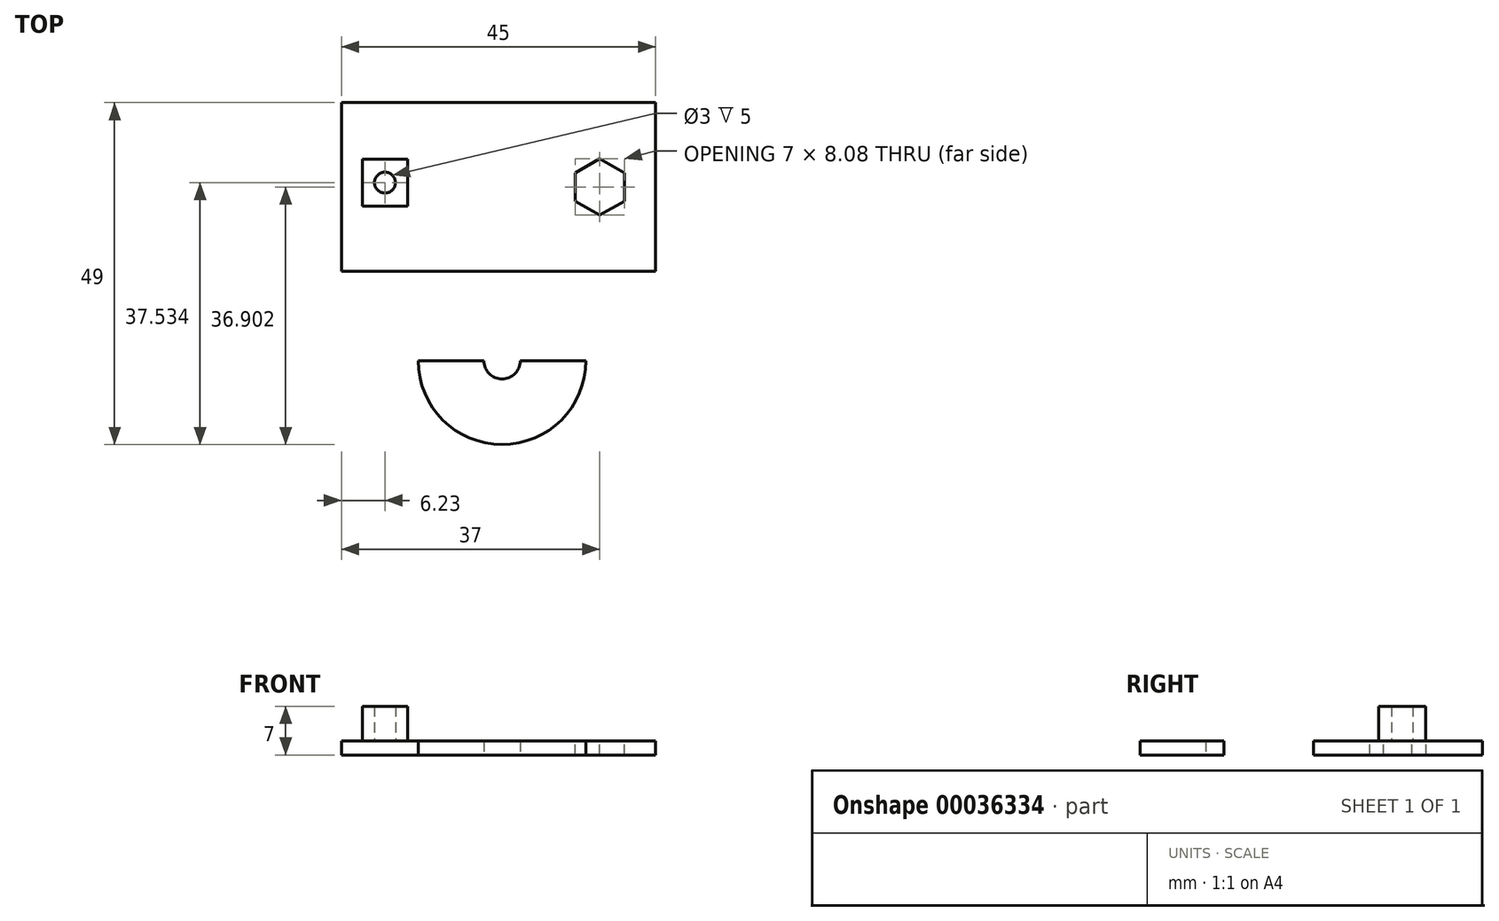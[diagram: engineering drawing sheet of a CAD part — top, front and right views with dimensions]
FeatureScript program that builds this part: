
annotation { "Feature Type Name" : "Feature", "Feature Type Description" : "" }
export const myFeature = defineFeature(function(context is Context, id is Id, definition is map)
    precondition{}
    {
        {
            var Q0;
            Q0=qCreatedBy(makeId("Top.planeOp"),FACE);
            var sketch = newSketch(context, id + "F0", { "sketchPlane" : qUnion([Q0])});
            skLineSegment(sketch, "E0.bottom", {"start": v(-25.2, 29.8) * mm, "end": v(19.8, 29.8) * mm});
            skLineSegment(sketch, "E0.top", {"start": v(-25.2, 5.6) * mm, "end": v(19.8, 5.6) * mm});
            skLineSegment(sketch, "E0.left", {"start": v(-25.2, 29.8) * mm, "end": v(-25.2, 5.6) * mm});
            skLineSegment(sketch, "E0.right", {"start": v(19.8, 29.8) * mm, "end": v(19.8, 5.6) * mm});
            skLineSegment(sketch, "E1.bottom", {"start": v(-14.2, 5.6) * mm, "end": v(9.8, 5.6) * mm});
            skLineSegment(sketch, "E1.top", {"start": v(-14.2, -7.2) * mm, "end": v(9.8, -7.2) * mm});
            skLineSegment(sketch, "E1.left", {"start": v(-14.2, 5.6) * mm, "end": v(-14.2, -7.2) * mm});
            skLineSegment(sketch, "E1.right", {"start": v(9.8, 5.6) * mm, "end": v(9.8, -7.2) * mm});
            skArc(sketch, "E2", {"start": v(-14.2, -7.2) * mm, "mid": v(-2.2, -19.2) * mm, "end": v(9.8, -7.2) * mm});
            skCircle(sketch, "E3", {"center": v(-2.2, -7.2) * mm, "radius": 2.6 * mm});
            skSolve(sketch);
        }
        {
            var Q0;
            Q0=makeQuery(id+"F0.imprint","IMPRINT",FACE,{"disambiguationData":[TD([[makeQuery(id+"F0.imprint","IMPRINT",EDGE,{"derivedFrom":sQuery(id+"F0.wireOp",EDGE,"E0.bottom")}),-1.0]])]});
            var Q1;
            Q1=makeQuery(id+"F0.imprint","IMPRINT",FACE,{"disambiguationData":[TD([[makeQuery(id+"F0.imprint","IMPRINT",EDGE,{"derivedFrom":sQuery(id+"F0.wireOp",EDGE,"E1.bottom")}),-1.0]])]});
            var Q2;
            {var subQ4=sQuery(id+"F0.wireOp",EDGE,"E2");Q2=makeQuery(id+"F0.imprint","IMPRINT",FACE,{"disambiguationData":[TD([[makeQuery(id+"F0.imprint","IMPRINT",EDGE,{"derivedFrom":subQ4}),1.0]])]});}
            extrude(context, id + "F1", {"entities" : qUnion([Q0, Q1, Q2]), "depth" : 2 * mm});
        }
        {
            var Q0;
            Q0=makeQuery(id+"F1.opExtrude","CAP_FACE",FACE,{"disambiguationData":[OSD([sQuery(id+"F0.wireOp",EDGE,"E0.bottom"),sQuery(id+"F0.wireOp",EDGE,"E0.top"),sQuery(id+"F0.wireOp",EDGE,"E0.left"),sQuery(id+"F0.wireOp",EDGE,"E0.right"),sQuery(id+"F0.wireOp",EDGE,"E1.left"),sQuery(id+"F0.wireOp",EDGE,"E1.right"),sQuery(id+"F0.wireOp",EDGE,"E2"),sQuery(id+"F0.wireOp",EDGE,"E3")])],"isStart":false});
            var sketch = newSketch(context, id + "F2", { "sketchPlane" : qUnion([Q0])});
            skLineSegment(sketch, "E4.bottom", {"start": v(-22.2, 21.69) * mm, "end": v(-15.74, 21.69) * mm});
            skLineSegment(sketch, "E4.top", {"start": v(-22.2, 14.96) * mm, "end": v(-15.74, 14.96) * mm});
            skLineSegment(sketch, "E4.left", {"start": v(-22.2, 21.69) * mm, "end": v(-22.2, 14.96) * mm});
            skLineSegment(sketch, "E4.right", {"start": v(-15.74, 21.69) * mm, "end": v(-15.74, 14.96) * mm});
            skLineSegment(sketch, "E5", {"start": v(-18.97, 21.69) * mm, "end": v(-18.97, 18.32) * mm, "construction": true});
            skPoint(sketch, "E5.endSnap0", {"position": v(-15.74, 18.32) * mm});
            skLineSegment(sketch, "E6", {"start": v(-18.97, 18.32) * mm, "end": v(-18.97, 14.96) * mm, "construction": true});
            skCircle(sketch, "E7", {"center": v(-18.97, 18.32) * mm, "radius": 1.5 * mm});
            skSolve(sketch);
        }
        {
            var Q0;
            Q0=makeQuery(id+"F2.imprint","IMPRINT",FACE,{"disambiguationData":[TD([[makeQuery(id+"F2.imprint","IMPRINT",EDGE,{"derivedFrom":sQuery(id+"F2.wireOp",EDGE,"E4.bottom")}),-1.0]])]});
            extrude(context, id + "F3", {"entities" : qUnion([Q0]), "operationType" : NewBodyOperationType.ADD, "depth" : 5 * mm});
        }
        {
            var Q0;
            {var subQ0=sQuery(id+"F0.wireOp",EDGE,"E0.bottom");var subQ1=sQuery(id+"F0.wireOp",EDGE,"E0.top");var subQ2=sQuery(id+"F0.wireOp",EDGE,"E0.left");var subQ3=sQuery(id+"F0.wireOp",EDGE,"E0.right");var subQ4=sQuery(id+"F0.wireOp",EDGE,"E1.left");var subQ5=sQuery(id+"F0.wireOp",EDGE,"E1.right");var subQ6=sQuery(id+"F0.wireOp",EDGE,"E2");var subQ7=sQuery(id+"F0.wireOp",EDGE,"E3");Q0=makeQuery(id+"F3.boolean.opBoolean","SPLIT",FACE,{"disambiguationData":[TD([makeQuery(id+"F1.opExtrude","SWEPT_FACE",FACE,{"disambiguationData":[OSD([subQ0])]})])],"derivedFrom":makeQuery(id+"F1.opExtrude","CAP_FACE",FACE,{"disambiguationData":[OSD([subQ0,subQ1,subQ2,subQ3,subQ4,subQ5,subQ6,subQ7])],"isStart":false})});}
            var sketch = newSketch(context, id + "F4", { "sketchPlane" : qUnion([Q0])});
            skCircle(sketch, "E8", {"center": v(11.8, 17.7) * mm, "radius": 1.5 * mm});
            skPoint(sketch, "E8.centerSnap0", {"position": v(19.8, 17.7) * mm});
            skCircle(sketch, "E9.cCircle", {"center": v(11.8, 17.7) * mm, "radius": 3.5 * mm, "construction": true});
            skLineSegment(sketch, "E9.0", {"start": v(15.3, 19.71) * mm, "end": v(15.3, 15.67) * mm});
            skLineSegment(sketch, "E9.1", {"start": v(15.3, 15.67) * mm, "end": v(11.8, 13.65) * mm});
            skLineSegment(sketch, "E9.2", {"start": v(11.8, 13.65) * mm, "end": v(8.3, 15.67) * mm});
            skLineSegment(sketch, "E9.3", {"start": v(8.3, 15.67) * mm, "end": v(8.3, 19.71) * mm});
            skLineSegment(sketch, "E9.4", {"start": v(8.3, 19.71) * mm, "end": v(11.8, 21.73) * mm});
            skLineSegment(sketch, "E9.5", {"start": v(11.8, 21.73) * mm, "end": v(15.3, 19.71) * mm});
            skPoint(sketch, "E9.0.midPoint", {"position": v(15.3, 17.7) * mm});
            skSolve(sketch);
        }
        {
            var Q0;
            Q0=makeQuery(id+"F4.imprint","IMPRINT",FACE,{"disambiguationData":[TD([[makeQuery(id+"F4.imprint","IMPRINT",EDGE,{"derivedFrom":sQuery(id+"F4.wireOp",EDGE,"E8")}),1.0]])]});
            var Q1;
            Q1=makeQuery(id+"F4.imprint","IMPRINT",FACE,{"disambiguationData":[TD([[makeQuery(id+"F4.imprint","IMPRINT",EDGE,{"derivedFrom":sQuery(id+"F4.wireOp",EDGE,"E8")}),-1.0]])]});
            extrude(context, id + "F5", {"entities" : qUnion([Q0, Q1]), "operationType" : NewBodyOperationType.REMOVE, "endBound" : BoundingType.UP_TO_NEXT, "oppositeDirection" : true, "depth" : 1 * mm});
        }
    });
